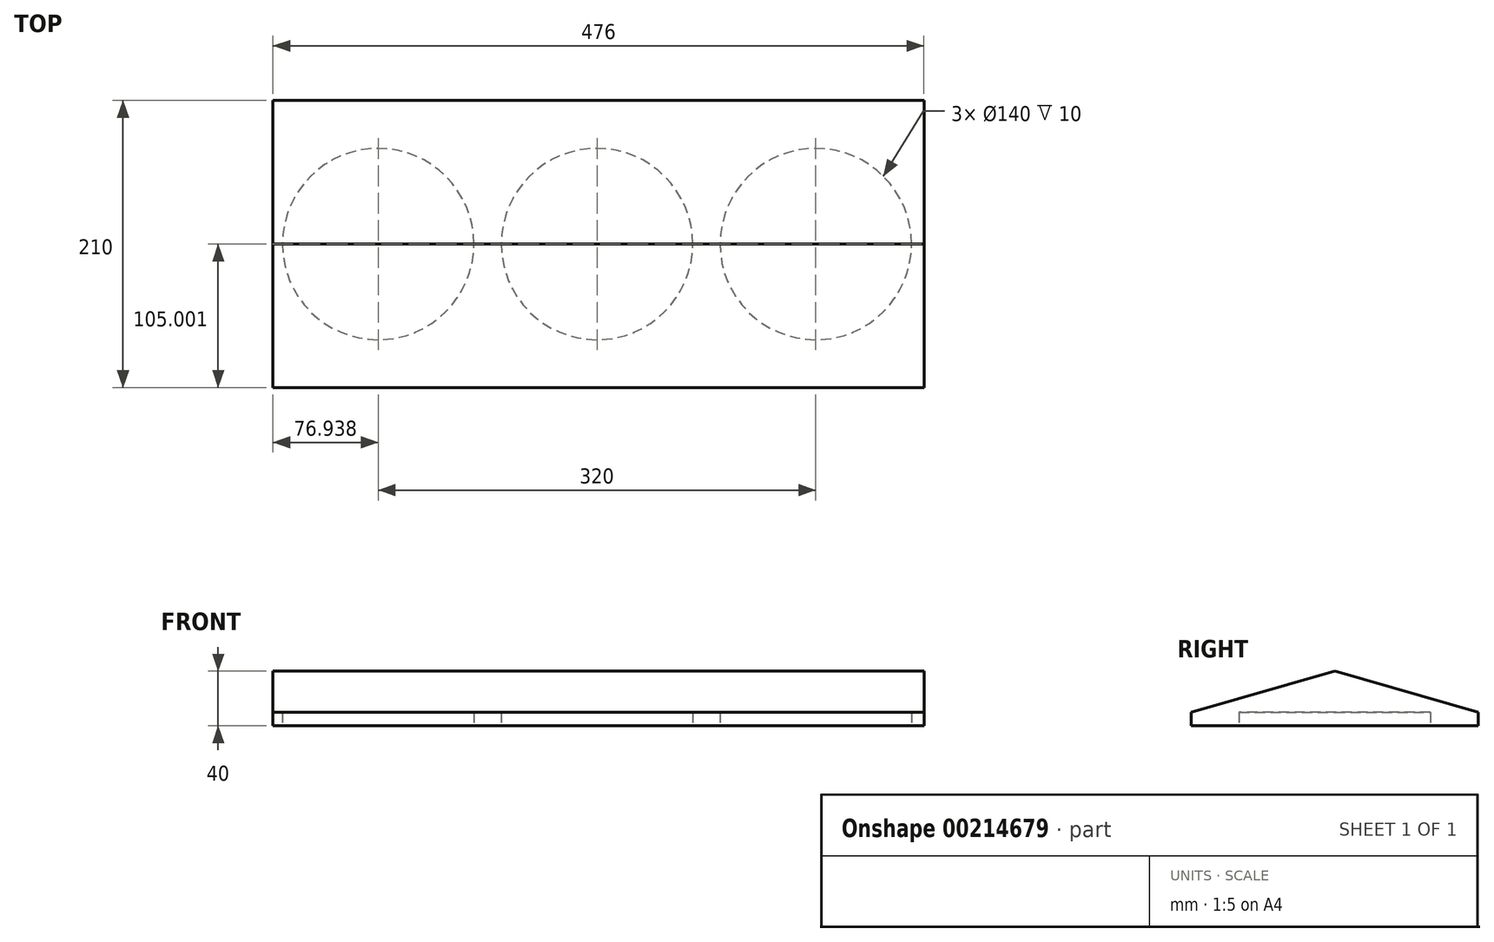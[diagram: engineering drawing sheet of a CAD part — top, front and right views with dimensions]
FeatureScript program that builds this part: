
annotation { "Feature Type Name" : "Feature", "Feature Type Description" : "" }
export const myFeature = defineFeature(function(context is Context, id is Id, definition is map)
    precondition{}
    {
        {
            var Q0;
            Q0=qCreatedBy(makeId("Top.planeOp"),FACE);
            var sketch = newSketch(context, id + "F0", { "sketchPlane" : qUnion([Q0])});
            skLineSegment(sketch, "E0.bottom", {"start": v(-328.74, 89.78) * mm, "end": v(147.26, 89.78) * mm});
            skLineSegment(sketch, "E0.top", {"start": v(-328.74, -120.22) * mm, "end": v(147.26, -120.22) * mm});
            skLineSegment(sketch, "E0.left", {"start": v(-328.74, 89.78) * mm, "end": v(-328.74, -120.22) * mm});
            skLineSegment(sketch, "E0.right", {"start": v(147.26, 89.78) * mm, "end": v(147.26, -120.22) * mm});
            skCircle(sketch, "E1", {"center": v(-91.8, -15.22) * mm, "radius": 70 * mm});
            skCircle(sketch, "E2", {"center": v(68.2, -15.22) * mm, "radius": 70 * mm});
            skCircle(sketch, "E3", {"center": v(-251.8, -15.22) * mm, "radius": 70 * mm});
            skSolve(sketch);
        }
        {
            var Q0;
            Q0=makeQuery(id+"F0.imprint","IMPRINT",FACE,{"disambiguationData":[TD([[makeQuery(id+"F0.imprint","IMPRINT",EDGE,{"derivedFrom":sQuery(id+"F0.wireOp",EDGE,"E0.bottom")}),-1.0]])]});
            extrude(context, id + "F1", {"entities" : qUnion([Q0]), "depth" : 10 * mm});
        }
        {
            var Q0;
            Q0=makeQuery(id+"F1.opExtrude","SWEPT_FACE",FACE,{"disambiguationData":[OSD([sQuery(id+"F0.wireOp",EDGE,"E0.right")])]});
            var sketch = newSketch(context, id + "F2", { "sketchPlane" : qUnion([Q0])});
            skLineSegment(sketch, "E4", {"start": v(-15.22, 10) * mm, "end": v(-15.22, 40) * mm});
            skLineSegment(sketch, "E5", {"start": v(-15.22, 40) * mm, "end": v(-120.22, 10) * mm});
            skLineSegment(sketch, "E6", {"start": v(-15.22, 40) * mm, "end": v(89.78, 10) * mm});
            skSolve(sketch);
        }
        {
            var Q0;
            {var subQ0=sQuery(id+"F2.wireOp",EDGE,"E4");Q0=makeQuery(id+"F2.imprint","IMPRINT",FACE,{"disambiguationData":[TD([[makeQuery(id+"F2.imprint","IMPRINT",EDGE,{"derivedFrom":subQ0}),1.0]])]});}
            var Q1;
            {var subQ0=sQuery(id+"F2.wireOp",EDGE,"E4");Q1=makeQuery(id+"F2.imprint","IMPRINT",FACE,{"disambiguationData":[TD([[makeQuery(id+"F2.imprint","IMPRINT",EDGE,{"derivedFrom":subQ0}),-1.0]])]});}
            extrude(context, id + "F3", {"entities" : qUnion([Q0, Q1]), "operationType" : NewBodyOperationType.ADD, "oppositeDirection" : true, "depth" : 476 * mm});
        }
    });
